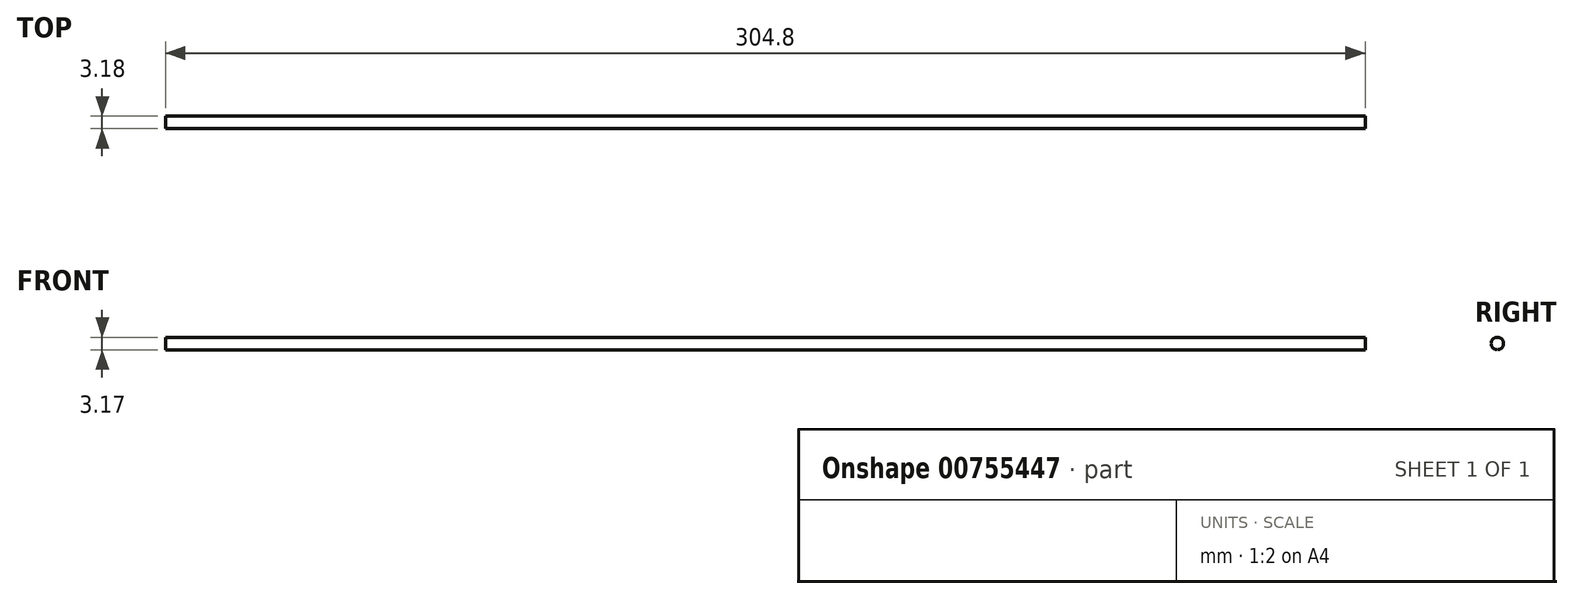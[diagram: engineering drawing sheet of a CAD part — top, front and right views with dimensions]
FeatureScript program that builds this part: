
annotation { "Feature Type Name" : "Feature", "Feature Type Description" : "" }
export const myFeature = defineFeature(function(context is Context, id is Id, definition is map)
    precondition{}
    {
        {
            var Q0;
            Q0=qCreatedBy(makeId("Right.planeOp"),FACE);
            var sketch = newSketch(context, id + "F0", { "sketchPlane" : qUnion([Q0])});
            skCircle(sketch, "E0", {"center": v(27.88, 20.13) * mm, "radius": 1.59 * mm});
            skSolve(sketch);
        }
        {
            var Q0;
            Q0 = qSketchRegion(id + "F0", true);
            extrude(context, id + "F1", {"entities" : qUnion([Q0]), "depth" : 304.8 * mm, "offsetDistance" : 25.4 * mm});
        }
    });
